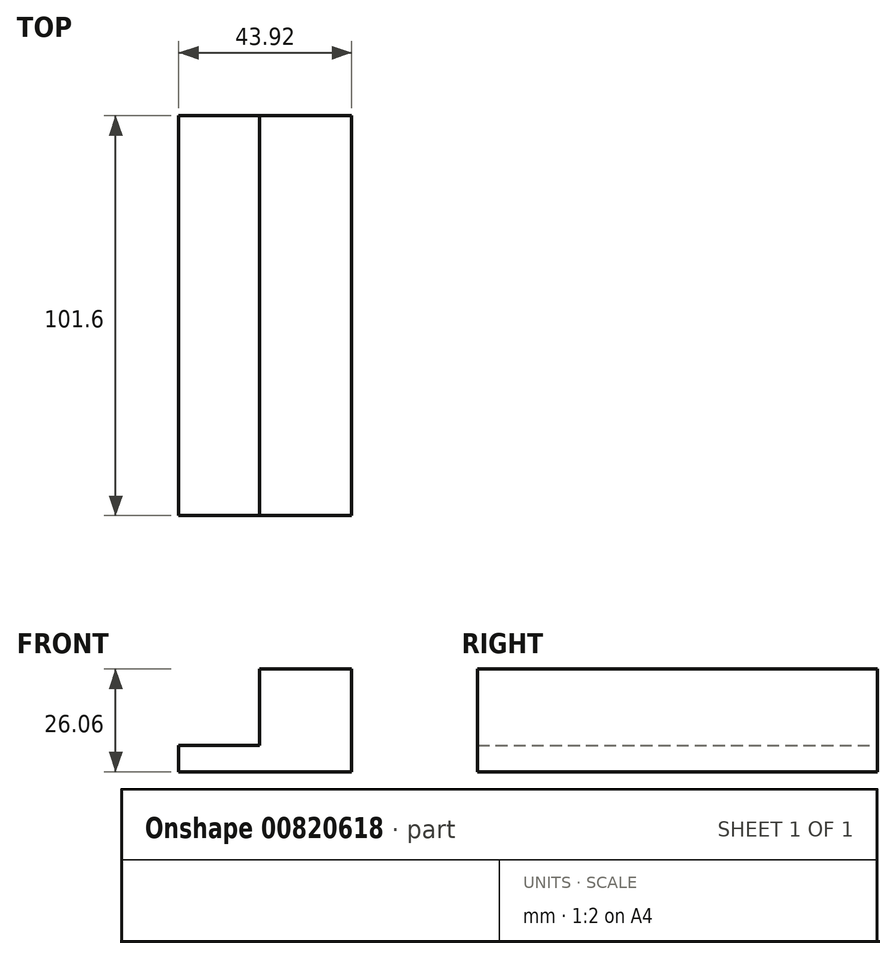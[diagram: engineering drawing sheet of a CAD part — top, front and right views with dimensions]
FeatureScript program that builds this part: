
annotation { "Feature Type Name" : "Feature", "Feature Type Description" : "" }
export const myFeature = defineFeature(function(context is Context, id is Id, definition is map)
    precondition{}
    {
        {
            var Q0;
            Q0=qCreatedBy(makeId("Front.planeOp"),FACE);
            var sketch = newSketch(context, id + "F0", { "sketchPlane" : qUnion([Q0])});
            skLineSegment(sketch, "E0", {"start": v(0, 0) * mm, "end": v(0, 26.06) * mm});
            skLineSegment(sketch, "E1", {"start": v(0, 26.06) * mm, "end": v(-23.37, 26.06) * mm});
            skLineSegment(sketch, "E2", {"start": v(-23.37, 26.06) * mm, "end": v(-23.37, 6.73) * mm});
            skLineSegment(sketch, "E3", {"start": v(-23.37, 6.73) * mm, "end": v(-43.92, 6.73) * mm});
            skLineSegment(sketch, "E4", {"start": v(-43.92, 6.73) * mm, "end": v(-43.92, 0) * mm});
            skLineSegment(sketch, "E5", {"start": v(-43.92, 0) * mm, "end": v(0, 0) * mm});
            skSolve(sketch);
        }
        {
            var Q0;
            Q0=makeQuery(id+"F0.imprint","IMPRINT",FACE,{"disambiguationData":[TD([[makeQuery(id+"F0.imprint","IMPRINT",EDGE,{"derivedFrom":sQuery(id+"F0.wireOp",EDGE,"E0")}),1.0]])]});
            extrude(context, id + "F1", {"entities" : qUnion([Q0]), "depth" : 101.6 * mm, "offsetDistance" : 25.4 * mm});
        }
    });
